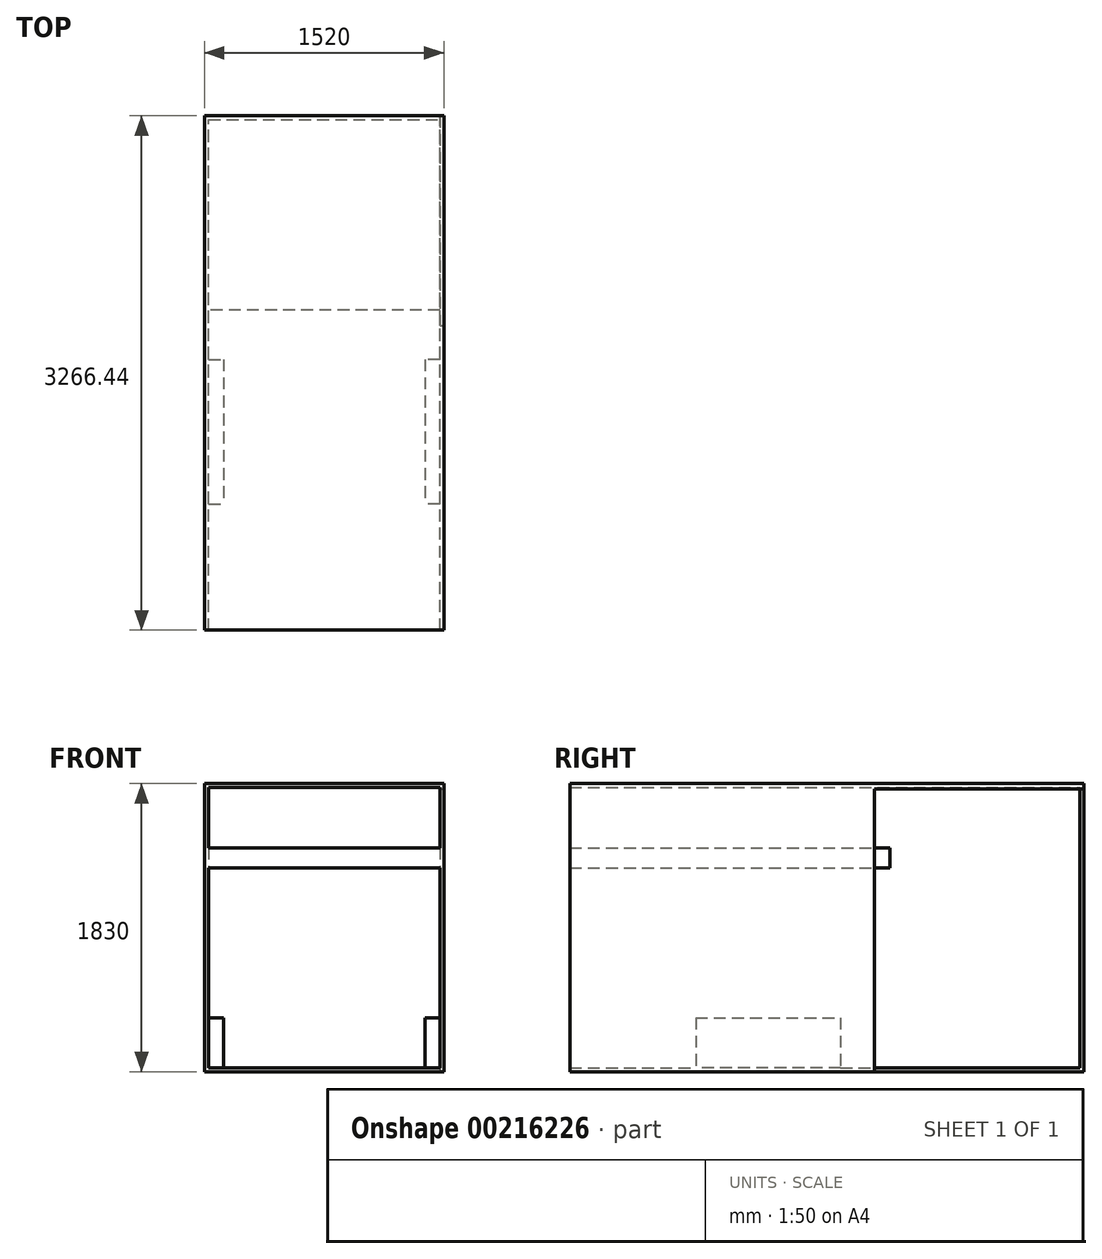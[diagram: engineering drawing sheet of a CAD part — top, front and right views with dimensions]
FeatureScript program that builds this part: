
annotation { "Feature Type Name" : "Feature", "Feature Type Description" : "" }
export const myFeature = defineFeature(function(context is Context, id is Id, definition is map)
    precondition{}
    {
        {
            var Q0;
            Q0=qCreatedBy(makeId("Front.planeOp"),FACE);
            var sketch = newSketch(context, id + "F0", { "sketchPlane" : qUnion([Q0])});
            skLineSegment(sketch, "E0.bottom", {"start": v(-760, 915) * mm, "end": v(760, 915) * mm});
            skLineSegment(sketch, "E0.top", {"start": v(-760, -915) * mm, "end": v(760, -915) * mm});
            skLineSegment(sketch, "E0.left", {"start": v(-760, 915) * mm, "end": v(-760, -915) * mm});
            skLineSegment(sketch, "E0.right", {"start": v(760, 915) * mm, "end": v(760, -915) * mm});
            skLineSegment(sketch, "E1", {"start": v(-760, 915) * mm, "end": v(760, -915) * mm});
            skSolve(sketch);
        }
        {
            var Q0;
            Q0=makeQuery(id+"F0.imprint","IMPRINT",FACE,{"disambiguationData":[TD([[makeQuery(id+"F0.imprint","IMPRINT",EDGE,{"derivedFrom":sQuery(id+"F0.wireOp",EDGE,"E0.bottom")}),-1.0]])]});
            var Q1;
            Q1=makeQuery(id+"F0.imprint","IMPRINT",FACE,{"disambiguationData":[TD([[makeQuery(id+"F0.imprint","IMPRINT",EDGE,{"derivedFrom":sQuery(id+"F0.wireOp",EDGE,"E0.top")}),1.0]])]});
            extrude(context, id + "F1", {"entities" : qUnion([Q0, Q1]), "depth" : 3266.44 * mm});
        }
        {
            var Q0;
            Q0=makeQuery(id+"F1.opExtrude","CAP_FACE",FACE,{"disambiguationData":[OSD([sQuery(id+"F0.wireOp",EDGE,"E0.bottom"),sQuery(id+"F0.wireOp",EDGE,"E0.top"),sQuery(id+"F0.wireOp",EDGE,"E0.left"),sQuery(id+"F0.wireOp",EDGE,"E0.right")])],"isStart":false});
            shell(context, id + "F2", {"entities" : qUnion([Q0]), "thickness" : 25.4 * mm});
        }
        {
            var Q0;
            Q0=makeQuery(id+"F2.opShell","OFFSET_FACE",FACE,{"disambiguationData":[OSD([sQuery(id+"F0.wireOp",EDGE,"E0.top")])]});
            var sketch = newSketch(context, id + "F3", { "sketchPlane" : qUnion([Q0])});
            skLineSegment(sketch, "E2.bottom", {"start": v(-734.6, -1546.96) * mm, "end": v(-640, -1546.96) * mm});
            skLineSegment(sketch, "E2.top", {"start": v(-734.6, -2466.44) * mm, "end": v(-640, -2466.44) * mm});
            skLineSegment(sketch, "E2.left", {"start": v(-734.6, -1546.96) * mm, "end": v(-734.6, -2466.44) * mm});
            skLineSegment(sketch, "E2.right", {"start": v(-640, -1546.96) * mm, "end": v(-640, -2466.44) * mm});
            skLineSegment(sketch, "E3.bottom", {"start": v(734.6, -1546.96) * mm, "end": v(640, -1546.96) * mm});
            skLineSegment(sketch, "E3.top", {"start": v(734.6, -2466.44) * mm, "end": v(640, -2466.44) * mm});
            skLineSegment(sketch, "E3.left", {"start": v(734.6, -1546.96) * mm, "end": v(734.6, -2466.44) * mm});
            skLineSegment(sketch, "E3.right", {"start": v(640, -1546.96) * mm, "end": v(640, -2466.44) * mm});
            skSolve(sketch);
        }
        {
            var Q0;
            Q0 = qSketchRegion(id + "F3", true);
            extrude(context, id + "F4", {"entities" : qUnion([Q0]), "operationType" : NewBodyOperationType.ADD, "depth" : 317.5 * mm});
        }
        {
            var Q0;
            Q0=makeQuery(id+"F2.opShell","OFFSET_FACE",FACE,{"disambiguationData":[OSD([sQuery(id+"F0.wireOp",EDGE,"E0.left")])]});
            var sketch = newSketch(context, id + "F5", { "sketchPlane" : qUnion([Q0])});
            skLineSegment(sketch, "E4.bottom", {"start": v(-3266.44, 507.4) * mm, "end": v(-1234.44, 507.4) * mm});
            skLineSegment(sketch, "E4.top", {"start": v(-3266.44, 380.4) * mm, "end": v(-1234.44, 380.4) * mm});
            skLineSegment(sketch, "E4.left", {"start": v(-3266.44, 507.4) * mm, "end": v(-3266.44, 380.4) * mm});
            skLineSegment(sketch, "E4.right", {"start": v(-1234.44, 507.4) * mm, "end": v(-1234.44, 380.4) * mm});
            skSolve(sketch);
        }
        {
            var Q0;
            Q0 = qSketchRegion(id + "F5", true);
            extrude(context, id + "F6", {"entities" : qUnion([Q0]), "operationType" : NewBodyOperationType.ADD, "endBound" : BoundingType.UP_TO_NEXT, "depth" : 25.4 * mm});
        }
        {
            var Q0;
            Q0=makeQuery(id+"F1.opExtrude","SWEPT_FACE",FACE,{"disambiguationData":[OSD([sQuery(id+"F0.wireOp",EDGE,"E0.right")])]});
            var sketch = newSketch(context, id + "F7", { "sketchPlane" : qUnion([Q0])});
            skLineSegment(sketch, "E5.bottom", {"start": v(0, -915) * mm, "end": v(-1331.06, -915) * mm});
            skLineSegment(sketch, "E5.top", {"start": v(0, 882.01) * mm, "end": v(-1331.06, 882.01) * mm});
            skLineSegment(sketch, "E5.left", {"start": v(0, -915) * mm, "end": v(0, 882.01) * mm});
            skLineSegment(sketch, "E5.right", {"start": v(-1331.06, -915) * mm, "end": v(-1331.06, 882.01) * mm});
            skSolve(sketch);
        }
        {
            var Q0;
            Q0=makeQuery(id+"F7.imprint","IMPRINT",FACE,{"disambiguationData":[TD([[makeQuery(id+"F7.imprint","IMPRINT",EDGE,{"derivedFrom":sQuery(id+"F7.wireOp",EDGE,"E5.bottom")}),1.0]])]});
            var Q1;
            Q1=makeQuery(id+"F2.opShell","OFFSET_FACE",FACE,{"disambiguationData":[OSD([sQuery(id+"F0.wireOp",EDGE,"E0.right")])]});
            extrude(context, id + "F8", {"entities" : qUnion([Q0]), "operationType" : NewBodyOperationType.REMOVE, "endBound" : BoundingType.UP_TO_SURFACE, "oppositeDirection" : true, "endBoundEntityFace" : qUnion([Q1]), "depth" : 25.4 * mm});
        }
    });
